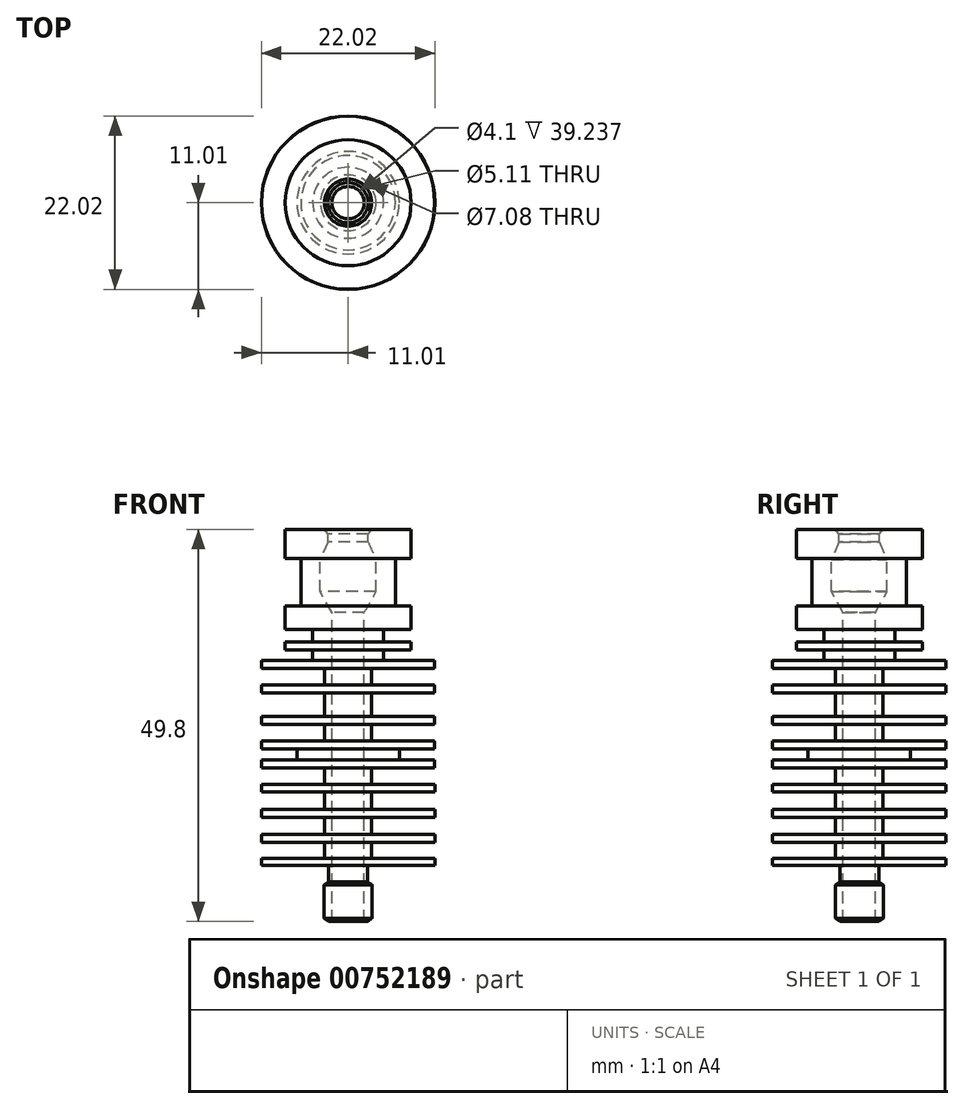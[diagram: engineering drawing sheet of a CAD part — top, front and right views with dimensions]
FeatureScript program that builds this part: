
annotation { "Feature Type Name" : "Feature", "Feature Type Description" : "" }
export const myFeature = defineFeature(function(context is Context, id is Id, definition is map)
    precondition{}
    {
        {
            var Q0;
            Q0=qCreatedBy(makeId("Front.planeOp"),FACE);
            var sketch = newSketch(context, id + "F0", { "sketchPlane" : qUnion([Q0])});
            skLineSegment(sketch, "E0", {"start": v(0, 61.45) * mm, "end": v(0, -25.18) * mm, "construction": true});
            skPoint(sketch, "E1", {"position": v(0, 49.8) * mm});
            skPoint(sketch, "E2", {"position": v(0, 7.1) * mm});
            skLineSegment(sketch, "E3", {"start": v(0, 49.8) * mm, "end": v(8, 49.8) * mm});
            skLineSegment(sketch, "E4", {"start": v(8, 49.8) * mm, "end": v(8, 46.1) * mm});
            skLineSegment(sketch, "E5", {"start": v(8, 46.1) * mm, "end": v(6, 46.1) * mm});
            skLineSegment(sketch, "E6", {"start": v(6, 46.1) * mm, "end": v(6, 40.1) * mm});
            skLineSegment(sketch, "E7", {"start": v(6, 40.1) * mm, "end": v(8, 40.1) * mm});
            skLineSegment(sketch, "E8", {"start": v(8, 40.1) * mm, "end": v(8, 37.1) * mm});
            skLineSegment(sketch, "E9", {"start": v(8, 37.1) * mm, "end": v(4.5, 37.1) * mm});
            skLineSegment(sketch, "E10", {"start": v(4.5, 37.1) * mm, "end": v(4.5, 35.52) * mm});
            skLineSegment(sketch, "E11", {"start": v(4.5, 35.52) * mm, "end": v(8, 35.52) * mm});
            skLineSegment(sketch, "E12", {"start": v(8, 35.52) * mm, "end": v(8, 34.52) * mm});
            skLineSegment(sketch, "E13", {"start": v(8, 34.52) * mm, "end": v(4.5, 34.52) * mm});
            skLineSegment(sketch, "E14", {"start": v(4.5, 34.52) * mm, "end": v(4.5, 33.13) * mm});
            skLineSegment(sketch, "E15", {"start": v(4.5, 33.13) * mm, "end": v(11, 33.13) * mm});
            skLineSegment(sketch, "E16", {"start": v(11, 33.13) * mm, "end": v(11, 32.13) * mm});
            skLineSegment(sketch, "E17", {"start": v(11, 32.13) * mm, "end": v(3, 32.13) * mm});
            skLineSegment(sketch, "E18", {"start": v(3, 32.13) * mm, "end": v(3, 30.03) * mm});
            skLineSegment(sketch, "E19", {"start": v(3, 30.03) * mm, "end": v(11, 30.03) * mm});
            skLineSegment(sketch, "E20", {"start": v(11, 30.03) * mm, "end": v(11, 29.03) * mm});
            skLineSegment(sketch, "E21", {"start": v(11, 29.03) * mm, "end": v(3, 29.03) * mm});
            skLineSegment(sketch, "E22", {"start": v(3, 29.03) * mm, "end": v(3, 26.03) * mm});
            skLineSegment(sketch, "E23", {"start": v(3, 26.03) * mm, "end": v(11, 26.03) * mm});
            skLineSegment(sketch, "E24", {"start": v(11, 26.03) * mm, "end": v(11, 25.03) * mm});
            skLineSegment(sketch, "E25", {"start": v(11, 25.03) * mm, "end": v(3, 25.03) * mm});
            skLineSegment(sketch, "E26", {"start": v(3, 25.03) * mm, "end": v(3, 22.93) * mm});
            skLineSegment(sketch, "E27", {"start": v(3, 22.93) * mm, "end": v(11, 22.93) * mm});
            skLineSegment(sketch, "E28", {"start": v(11, 22.93) * mm, "end": v(11, 21.93) * mm});
            skLineSegment(sketch, "E29", {"start": v(11, 21.93) * mm, "end": v(6.5, 21.93) * mm});
            skLineSegment(sketch, "E30", {"start": v(6.5, 21.93) * mm, "end": v(6.5, 20.53) * mm});
            skLineSegment(sketch, "E31", {"start": v(6.5, 20.53) * mm, "end": v(11, 20.53) * mm});
            skLineSegment(sketch, "E32", {"start": v(11, 20.53) * mm, "end": v(11, 19.53) * mm});
            skLineSegment(sketch, "E33", {"start": v(11, 19.53) * mm, "end": v(3, 19.53) * mm});
            skLineSegment(sketch, "E34", {"start": v(3, 19.53) * mm, "end": v(3, 17.43) * mm});
            skLineSegment(sketch, "E35", {"start": v(3, 17.43) * mm, "end": v(11.01, 17.43) * mm});
            skLineSegment(sketch, "E36", {"start": v(11.01, 17.43) * mm, "end": v(11.01, 16.43) * mm});
            skLineSegment(sketch, "E37", {"start": v(11.01, 16.43) * mm, "end": v(3, 16.43) * mm});
            skLineSegment(sketch, "E38", {"start": v(3, 16.43) * mm, "end": v(3, 14.23) * mm});
            skLineSegment(sketch, "E39", {"start": v(3, 14.23) * mm, "end": v(11.01, 14.23) * mm});
            skLineSegment(sketch, "E40", {"start": v(11.01, 14.23) * mm, "end": v(11.01, 13.23) * mm});
            skLineSegment(sketch, "E41", {"start": v(11.01, 13.23) * mm, "end": v(3, 13.23) * mm});
            skLineSegment(sketch, "E42", {"start": v(3, 13.23) * mm, "end": v(3, 11.03) * mm});
            skLineSegment(sketch, "E43", {"start": v(3, 11.03) * mm, "end": v(11.01, 11.03) * mm});
            skLineSegment(sketch, "E44", {"start": v(11.01, 11.03) * mm, "end": v(11.01, 10.03) * mm});
            skLineSegment(sketch, "E45", {"start": v(11.01, 10.03) * mm, "end": v(3, 10.03) * mm});
            skLineSegment(sketch, "E46", {"start": v(3, 10.03) * mm, "end": v(3, 8.03) * mm});
            skLineSegment(sketch, "E47", {"start": v(3, 8.03) * mm, "end": v(11.01, 8.03) * mm});
            skLineSegment(sketch, "E48", {"start": v(11.01, 8.03) * mm, "end": v(11.01, 7.1) * mm});
            skLineSegment(sketch, "E49", {"start": v(2.48, 7.1) * mm, "end": v(11.01, 7.1) * mm});
            skLineSegment(sketch, "E50", {"start": v(0, 49.8) * mm, "end": v(0, 7.1) * mm});
            skPoint(sketch, "E51", {"position": v(2.05, 7.1) * mm});
            skLineSegment(sketch, "E52", {"start": v(2.05, 7.1) * mm, "end": v(2.05, 0) * mm});
            skLineSegment(sketch, "E53", {"start": v(2.05, 7.1) * mm, "end": v(2.05, 39.24) * mm});
            skLineSegment(sketch, "E54", {"start": v(2.05, 39.24) * mm, "end": v(3.54, 41.9) * mm});
            skLineSegment(sketch, "E55", {"start": v(3.54, 41.9) * mm, "end": v(3.54, 45.97) * mm});
            skLineSegment(sketch, "E56", {"start": v(3.54, 45.97) * mm, "end": v(2.56, 48.21) * mm});
            skLineSegment(sketch, "E57", {"start": v(2.56, 48.21) * mm, "end": v(2.56, 49.21) * mm});
            skLineSegment(sketch, "E58", {"start": v(2.56, 49.21) * mm, "end": v(3, 49.8) * mm});
            skLineSegment(sketch, "E59", {"start": v(2.48, 7.1) * mm, "end": v(2.48, 5) * mm});
            skLineSegment(sketch, "E60", {"start": v(2.48, 5) * mm, "end": v(3.05, 4.67) * mm});
            skLineSegment(sketch, "E61", {"start": v(3.05, 4.67) * mm, "end": v(3.05, 0.4) * mm});
            skLineSegment(sketch, "E62", {"start": v(3.05, 0.4) * mm, "end": v(2.48, 0) * mm});
            skLineSegment(sketch, "E63", {"start": v(2.48, 0) * mm, "end": v(2.05, 0) * mm});
            skPoint(sketch, "E64", {"position": v(0, 0) * mm});
            skSolve(sketch);
        }
        {
            var Q0;
            {var subQ1=sQuery(id+"F0.wireOp",EDGE,"E4");Q0=makeQuery(id+"F0.imprint","IMPRINT",FACE,{"disambiguationData":[TD([[makeQuery(id+"F0.imprint","IMPRINT",EDGE,{"derivedFrom":subQ1}),-1.0]])]});}
            var Q1;
            Q1=sQuery(id+"F0.wireOp",EDGE,"E0");
            revolve(context, id + "F1", {"surfaceOperationType" : NewSurfaceOperationType.NEW, "entities" : qUnion([Q0]), "axis" : qUnion([Q1]), "revolveType" : RevolveType.FULL});
        }
    });
